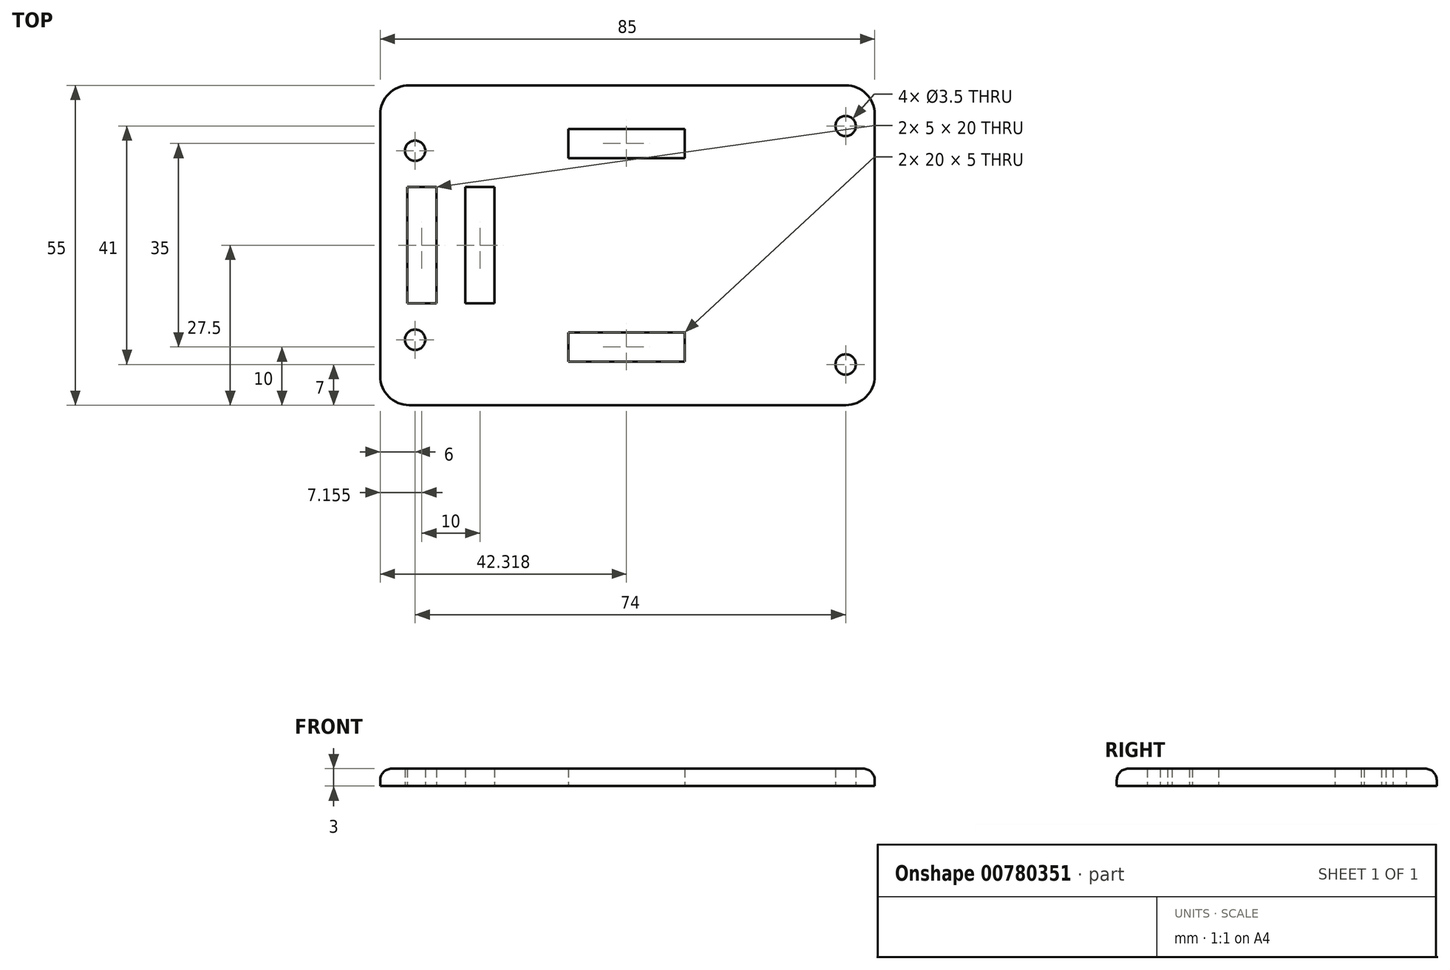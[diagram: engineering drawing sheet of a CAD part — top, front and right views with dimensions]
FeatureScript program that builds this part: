
annotation { "Feature Type Name" : "Feature", "Feature Type Description" : "" }
export const myFeature = defineFeature(function(context is Context, id is Id, definition is map)
    precondition{}
    {
        {
            var Q0;
            Q0=qCreatedBy(makeId("Top.planeOp"),FACE);
            var sketch = newSketch(context, id + "F0", { "sketchPlane" : qUnion([Q0])});
            skLineSegment(sketch, "E0", {"start": v(-5, 27.5) * mm, "end": v(-80, 27.5) * mm});
            skLineSegment(sketch, "E1", {"start": v(-85, 22.5) * mm, "end": v(-85, -22.5) * mm});
            skLineSegment(sketch, "E2", {"start": v(-80, -27.5) * mm, "end": v(-5, -27.5) * mm});
            skLineSegment(sketch, "E3", {"start": v(0, -22.5) * mm, "end": v(0, 22.5) * mm});
            skCircle(sketch, "E4", {"center": v(-5, 20.5) * mm, "radius": 1.75 * mm});
            skCircle(sketch, "E5.MirrorC", {"center": v(-5, -20.5) * mm, "radius": 1.75 * mm});
            skCircle(sketch, "E6", {"center": v(-79, 16.25) * mm, "radius": 1.75 * mm});
            skCircle(sketch, "E7.MirrorC", {"center": v(-79, -16.25) * mm, "radius": 1.75 * mm});
            skPoint(sketch, "E8.visualSharp", {"position": v(-85, 27.5) * mm});
            skArc(sketch, "E8.filletArc", {"start": v(-80, 27.5) * mm, "mid": v(-83.54, 26.04) * mm, "end": v(-85, 22.5) * mm});
            skPoint(sketch, "E9.visualSharp", {"position": v(-85, -27.5) * mm});
            skArc(sketch, "E9.filletArc", {"start": v(-85, -22.5) * mm, "mid": v(-83.54, -26.04) * mm, "end": v(-80, -27.5) * mm});
            skPoint(sketch, "E10.visualSharp", {"position": v(0, -27.5) * mm});
            skArc(sketch, "E10.filletArc", {"start": v(-5, -27.5) * mm, "mid": v(-1.46, -26.04) * mm, "end": v(0, -22.5) * mm});
            skPoint(sketch, "E11.visualSharp", {"position": v(0, 27.5) * mm});
            skArc(sketch, "E11.filletArc", {"start": v(0, 22.5) * mm, "mid": v(-1.46, 26.04) * mm, "end": v(-5, 27.5) * mm});
            skLineSegment(sketch, "E12.bottom", {"start": v(-52.68, 20) * mm, "end": v(-32.68, 20) * mm});
            skLineSegment(sketch, "E12.top", {"start": v(-52.68, 15) * mm, "end": v(-32.68, 15) * mm});
            skLineSegment(sketch, "E12.left", {"start": v(-52.68, 20) * mm, "end": v(-52.68, 15) * mm});
            skLineSegment(sketch, "E12.right", {"start": v(-32.68, 20) * mm, "end": v(-32.68, 15) * mm});
            skLineSegment(sketch, "E13.MirrorCS", {"start": v(-32.68, -20) * mm, "end": v(-32.68, -15) * mm});
            skLineSegment(sketch, "E14.MirrorCS", {"start": v(-52.68, -15) * mm, "end": v(-32.68, -15) * mm});
            skLineSegment(sketch, "E15.MirrorCS", {"start": v(-52.68, -20) * mm, "end": v(-32.68, -20) * mm});
            skLineSegment(sketch, "E16.MirrorCS", {"start": v(-52.68, -20) * mm, "end": v(-52.68, -15) * mm});
            skLineSegment(sketch, "E17.bottom", {"start": v(-80.34, 10) * mm, "end": v(-75.34, 10) * mm});
            skLineSegment(sketch, "E17.top", {"start": v(-80.34, -10) * mm, "end": v(-75.34, -10) * mm});
            skLineSegment(sketch, "E17.left", {"start": v(-80.34, 10) * mm, "end": v(-80.34, -10) * mm});
            skLineSegment(sketch, "E17.right", {"start": v(-75.34, 10) * mm, "end": v(-75.34, -10) * mm});
            skPoint(sketch, "E18.firstSnap0", {"position": v(-77.84, 10) * mm});
            skLineSegment(sketch, "E18.bottom", {"start": v(-70.34, 10) * mm, "end": v(-65.34, 10) * mm});
            skLineSegment(sketch, "E18.top", {"start": v(-70.34, -10) * mm, "end": v(-65.34, -10) * mm});
            skLineSegment(sketch, "E18.left", {"start": v(-70.34, 10) * mm, "end": v(-70.34, -10) * mm});
            skLineSegment(sketch, "E18.right", {"start": v(-65.34, 10) * mm, "end": v(-65.34, -10) * mm});
            skSolve(sketch);
        }
        {
            var Q0;
            Q0=makeQuery(id+"F0.imprint","IMPRINT",FACE,{"disambiguationData":[TD([[makeQuery(id+"F0.imprint","IMPRINT",EDGE,{"derivedFrom":sQuery(id+"F0.wireOp",EDGE,"E0")}),1.0]])]});
            extrude(context, id + "F1", {"entities" : qUnion([Q0]), "depth" : 3 * mm, "offsetDistance" : 25.4 * mm});
        }
        {
            var Q0;
            Q0=makeQuery(id+"F1.opExtrude","CAP_EDGE",EDGE,{"disambiguationData":[OSD([sQuery(id+"F0.wireOp",EDGE,"E1")])],"isStart":false});
            fillet(context, id + "F2", {"entities" : qUnion([Q0]), "radius" : 2 * mm, "tangentPropagation" : true, "allowEdgeOverflow" : false});
        }
    });
